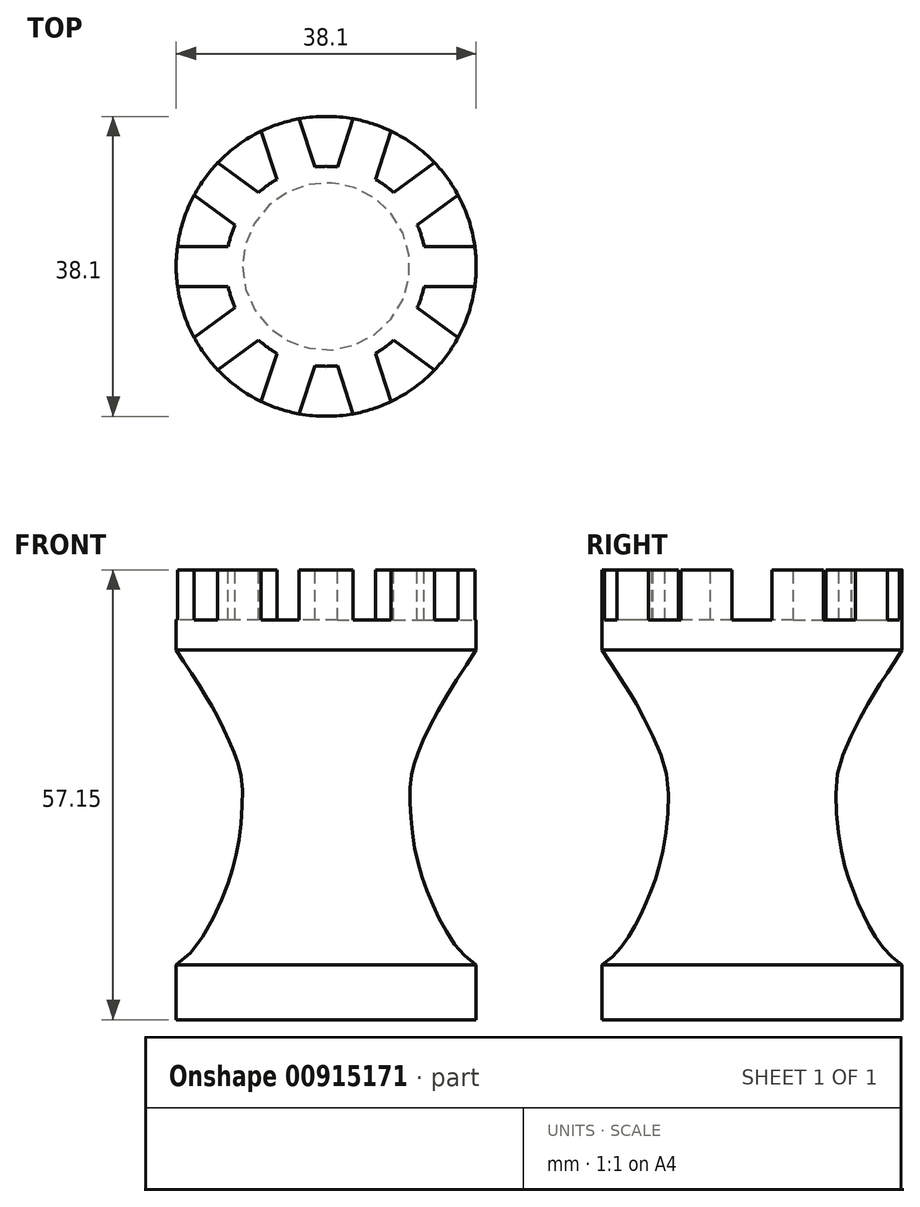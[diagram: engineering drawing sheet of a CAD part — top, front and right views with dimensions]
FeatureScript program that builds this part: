
annotation { "Feature Type Name" : "Feature", "Feature Type Description" : "" }
export const myFeature = defineFeature(function(context is Context, id is Id, definition is map)
    precondition{}
    {
        {
            var Q0;
            Q0=qCreatedBy(makeId("Front.planeOp"),FACE);
            var sketch = newSketch(context, id + "F0", { "sketchPlane" : qUnion([Q0])});
            skLineSegment(sketch, "E0", {"start": v(0, 0) * mm, "end": v(0, 57.15) * mm});
            skLineSegment(sketch, "E1", {"start": v(0, 0) * mm, "end": v(19.05, 0) * mm});
            skLineSegment(sketch, "E2", {"start": v(19.05, 0) * mm, "end": v(19.05, 6.99) * mm});
            skLineSegment(sketch, "E3", {"start": v(0, 47) * mm, "end": v(24.3, 47) * mm, "construction": true});
            skFitSpline(sketch, "E4", {"points": [v(19.05, 6.99) * mm, v(12.97, 16.04) * mm, v(11.14, 22.45) * mm, v(10.7, 30.04) * mm, v(11.81, 34.28) * mm, v(13.82, 38.51) * mm, v(16.05, 42.3) * mm, v(19.05, 47) * mm], "startDerivative": vector(-44.31, 25.16) * mm, "endDerivative": vector(20.66, 33.84) * mm});
            skLineSegment(sketch, "E5.bottom", {"start": v(0, 47) * mm, "end": v(19.05, 47) * mm});
            skLineSegment(sketch, "E5.top", {"start": v(0, 57.15) * mm, "end": v(19.05, 57.15) * mm});
            skLineSegment(sketch, "E5.left", {"start": v(0, 47) * mm, "end": v(0, 57.15) * mm});
            skLineSegment(sketch, "E5.right", {"start": v(19.05, 47) * mm, "end": v(19.05, 57.15) * mm});
            skSolve(sketch);
        }
        {
            var Q0;
            Q0 = qSketchRegion(id + "F0", true);
            var Q1;
            Q1=sQuery(id+"F0.wireOp",EDGE,"E0");
            revolve(context, id + "F1", {"surfaceOperationType" : NewSurfaceOperationType.NEW, "entities" : qUnion([Q0]), "axis" : qUnion([Q1]), "revolveType" : RevolveType.FULL});
        }
        {
            var Q0;
            Q0=makeQuery(id+"F1.opRevolve","SWEPT_FACE",FACE,{"disambiguationData":[OSD([sQuery(id+"F0.wireOp",EDGE,"E5.top")])]});
            var sketch = newSketch(context, id + "F2", { "sketchPlane" : qUnion([Q0])});
            skCircle(sketch, "E6", {"center": v(0, 0) * mm, "radius": 12.7 * mm});
            skSolve(sketch);
        }
        {
            var Q0;
            Q0=makeQuery(id+"F2.imprint","IMPRINT",FACE,{"disambiguationData":[TD([[makeQuery(id+"F2.imprint","IMPRINT",EDGE,{"derivedFrom":sQuery(id+"F2.wireOp",EDGE,"E6")}),1.0]])]});
            extrude(context, id + "F3", {"entities" : qUnion([Q0]), "operationType" : NewBodyOperationType.REMOVE, "oppositeDirection" : true, "depth" : 6.35 * mm, "offsetDistance" : 25.4 * mm});
        }
        {
            var Q0;
            Q0=makeQuery(id+"F1.opRevolve","SWEPT_FACE",FACE,{"disambiguationData":[OSD([sQuery(id+"F0.wireOp",EDGE,"E5.top")])]});
            var sketch = newSketch(context, id + "F4", { "sketchPlane" : qUnion([Q0])});
            skLineSegment(sketch, "E7", {"start": v(0, 0) * mm, "end": v(16.05, 0) * mm, "construction": true});
            skLineSegment(sketch, "E8.bottom", {"start": v(12.44, 2.54) * mm, "end": v(19.65, 2.54) * mm});
            skLineSegment(sketch, "E8.top", {"start": v(12.44, -2.54) * mm, "end": v(19.65, -2.54) * mm});
            skLineSegment(sketch, "E8.left", {"start": v(12.44, 2.54) * mm, "end": v(12.44, -2.54) * mm});
            skLineSegment(sketch, "E8.right", {"start": v(19.65, 2.54) * mm, "end": v(19.65, -2.54) * mm});
            skPoint(sketch, "E8.middle", {"position": v(16.05, 0) * mm});
            skLineSegment(sketch, "E9.1.0", {"start": v(8.57, 9.37) * mm, "end": v(11.56, 5.26) * mm});
            skLineSegment(sketch, "E9.1.1", {"start": v(14.4, 13.6) * mm, "end": v(17.39, 9.5) * mm});
            skLineSegment(sketch, "E9.1.2", {"start": v(8.57, 9.37) * mm, "end": v(14.4, 13.6) * mm});
            skPoint(sketch, "E9.1.3", {"position": v(12.98, 9.43) * mm});
            skLineSegment(sketch, "E9.1.4", {"start": v(11.56, 5.26) * mm, "end": v(17.39, 9.5) * mm});
            skLineSegment(sketch, "E9.2.0", {"start": v(1.43, 12.62) * mm, "end": v(6.26, 11.05) * mm});
            skLineSegment(sketch, "E9.2.1", {"start": v(3.66, 19.47) * mm, "end": v(8.49, 17.9) * mm});
            skLineSegment(sketch, "E9.2.2", {"start": v(1.43, 12.62) * mm, "end": v(3.66, 19.47) * mm});
            skPoint(sketch, "E9.2.3", {"position": v(4.96, 15.26) * mm});
            skLineSegment(sketch, "E9.2.4", {"start": v(6.26, 11.05) * mm, "end": v(8.49, 17.9) * mm});
            skLineSegment(sketch, "E9.3.0", {"start": v(-6.26, 11.05) * mm, "end": v(-1.43, 12.62) * mm});
            skLineSegment(sketch, "E9.3.1", {"start": v(-8.49, 17.9) * mm, "end": v(-3.66, 19.47) * mm});
            skLineSegment(sketch, "E9.3.2", {"start": v(-6.26, 11.05) * mm, "end": v(-8.49, 17.9) * mm});
            skPoint(sketch, "E9.3.3", {"position": v(-4.96, 15.26) * mm});
            skLineSegment(sketch, "E9.3.4", {"start": v(-1.43, 12.62) * mm, "end": v(-3.66, 19.47) * mm});
            skLineSegment(sketch, "E9.4.0", {"start": v(-11.56, 5.26) * mm, "end": v(-8.57, 9.37) * mm});
            skLineSegment(sketch, "E9.4.1", {"start": v(-17.39, 9.5) * mm, "end": v(-14.4, 13.6) * mm});
            skLineSegment(sketch, "E9.4.2", {"start": v(-11.56, 5.26) * mm, "end": v(-17.39, 9.5) * mm});
            skPoint(sketch, "E9.4.3", {"position": v(-12.98, 9.43) * mm});
            skLineSegment(sketch, "E9.4.4", {"start": v(-8.57, 9.37) * mm, "end": v(-14.4, 13.6) * mm});
            skLineSegment(sketch, "E9.5.0", {"start": v(-12.44, -2.54) * mm, "end": v(-12.44, 2.54) * mm});
            skLineSegment(sketch, "E9.5.1", {"start": v(-19.65, -2.54) * mm, "end": v(-19.65, 2.54) * mm});
            skLineSegment(sketch, "E9.5.2", {"start": v(-12.44, -2.54) * mm, "end": v(-19.65, -2.54) * mm});
            skPoint(sketch, "E9.5.3", {"position": v(-16.05, 0) * mm});
            skLineSegment(sketch, "E9.5.4", {"start": v(-12.44, 2.54) * mm, "end": v(-19.65, 2.54) * mm});
            skLineSegment(sketch, "E9.6.0", {"start": v(-8.57, -9.37) * mm, "end": v(-11.56, -5.26) * mm});
            skLineSegment(sketch, "E9.6.1", {"start": v(-14.4, -13.6) * mm, "end": v(-17.39, -9.5) * mm});
            skLineSegment(sketch, "E9.6.2", {"start": v(-8.57, -9.37) * mm, "end": v(-14.4, -13.6) * mm});
            skPoint(sketch, "E9.6.3", {"position": v(-12.98, -9.43) * mm});
            skLineSegment(sketch, "E9.6.4", {"start": v(-11.56, -5.26) * mm, "end": v(-17.39, -9.5) * mm});
            skLineSegment(sketch, "E9.7.0", {"start": v(-1.43, -12.62) * mm, "end": v(-6.26, -11.05) * mm});
            skLineSegment(sketch, "E9.7.1", {"start": v(-3.66, -19.47) * mm, "end": v(-8.49, -17.9) * mm});
            skLineSegment(sketch, "E9.7.2", {"start": v(-1.43, -12.62) * mm, "end": v(-3.66, -19.47) * mm});
            skPoint(sketch, "E9.7.3", {"position": v(-4.96, -15.26) * mm});
            skLineSegment(sketch, "E9.7.4", {"start": v(-6.26, -11.05) * mm, "end": v(-8.49, -17.9) * mm});
            skLineSegment(sketch, "E9.8.0", {"start": v(6.26, -11.05) * mm, "end": v(1.43, -12.62) * mm});
            skLineSegment(sketch, "E9.8.1", {"start": v(8.49, -17.9) * mm, "end": v(3.66, -19.47) * mm});
            skLineSegment(sketch, "E9.8.2", {"start": v(6.26, -11.05) * mm, "end": v(8.49, -17.9) * mm});
            skPoint(sketch, "E9.8.3", {"position": v(4.96, -15.26) * mm});
            skLineSegment(sketch, "E9.8.4", {"start": v(1.43, -12.62) * mm, "end": v(3.66, -19.47) * mm});
            skLineSegment(sketch, "E9.9.0", {"start": v(11.56, -5.26) * mm, "end": v(8.57, -9.37) * mm});
            skLineSegment(sketch, "E9.9.1", {"start": v(17.39, -9.5) * mm, "end": v(14.4, -13.6) * mm});
            skLineSegment(sketch, "E9.9.2", {"start": v(11.56, -5.26) * mm, "end": v(17.39, -9.5) * mm});
            skPoint(sketch, "E9.9.3", {"position": v(12.98, -9.43) * mm});
            skLineSegment(sketch, "E9.9.4", {"start": v(8.57, -9.37) * mm, "end": v(14.4, -13.6) * mm});
            skPoint(sketch, "E9.center", {"position": v(0, 0) * mm});
            skSolve(sketch);
        }
        {
            var Q0;
            Q0 = qSketchRegion(id + "F4", true);
            extrude(context, id + "F5", {"entities" : qUnion([Q0]), "operationType" : NewBodyOperationType.REMOVE, "oppositeDirection" : true, "depth" : 6.35 * mm, "offsetDistance" : 25.4 * mm});
        }
    });
